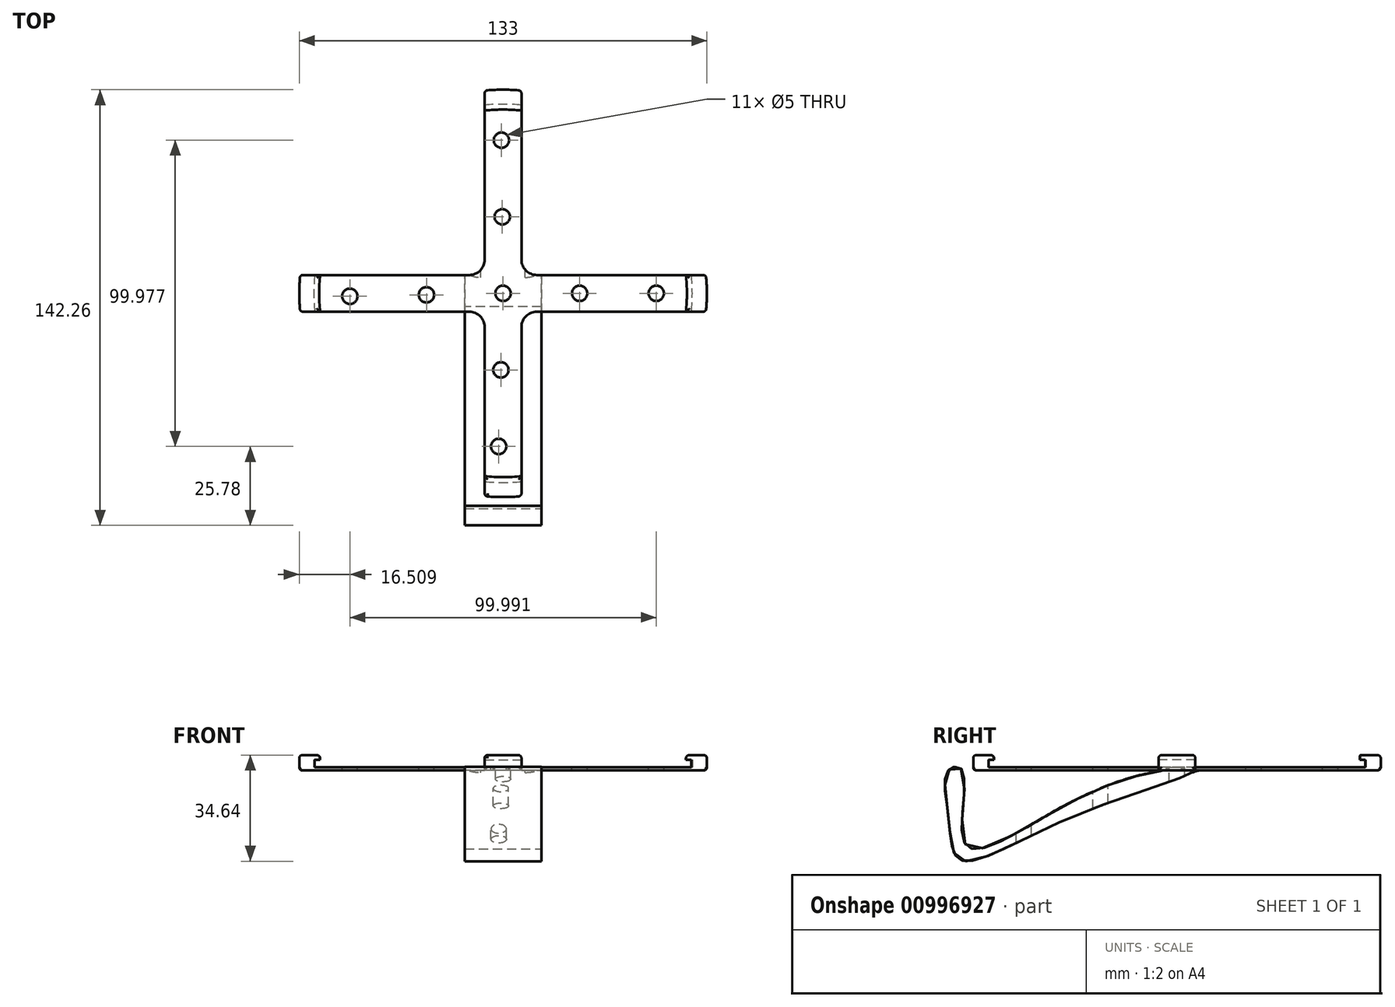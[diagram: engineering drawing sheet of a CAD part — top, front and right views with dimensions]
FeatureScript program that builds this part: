
annotation { "Feature Type Name" : "Feature", "Feature Type Description" : "" }
export const myFeature = defineFeature(function(context is Context, id is Id, definition is map)
    precondition{}
    {
        {
            var Q0;
            Q0=qCreatedBy(makeId("Top.planeOp"),FACE);
            var sketch = newSketch(context, id + "F0", { "sketchPlane" : qUnion([Q0])});
            skCircle(sketch, "E0", {"center": v(0, 0) * mm, "radius": 66.5 * mm, "construction": true});
            skLineSegment(sketch, "E1.bottom", {"start": v(6, -6) * mm, "end": v(-6, -6) * mm, "construction": true});
            skLineSegment(sketch, "E1.top", {"start": v(6, 6) * mm, "end": v(-6, 6) * mm, "construction": true});
            skLineSegment(sketch, "E1.left", {"start": v(6, -6) * mm, "end": v(6, 6) * mm, "construction": true});
            skLineSegment(sketch, "E1.right", {"start": v(-6, -6) * mm, "end": v(-6, 6) * mm, "construction": true});
            skLineSegment(sketch, "E2", {"start": v(-6, 6) * mm, "end": v(-66.23, 6) * mm});
            skLineSegment(sketch, "E3", {"start": v(-6, -6) * mm, "end": v(-66.23, -6) * mm});
            skArc(sketch, "E4", {"start": v(-66.23, 6) * mm, "mid": v(-66.5, 0) * mm, "end": v(-66.23, -6) * mm});
            skLineSegment(sketch, "E5.1.0", {"start": v(-6, -6) * mm, "end": v(-6, -66.23) * mm});
            skLineSegment(sketch, "E5.1.1", {"start": v(6, -6) * mm, "end": v(6, -66.23) * mm});
            skArc(sketch, "E5.1.2", {"start": v(-6, -66.23) * mm, "mid": v(0, -66.5) * mm, "end": v(6, -66.23) * mm});
            skLineSegment(sketch, "E5.2.0", {"start": v(6, -6) * mm, "end": v(66.23, -6) * mm});
            skLineSegment(sketch, "E5.2.1", {"start": v(6, 6) * mm, "end": v(66.23, 6) * mm});
            skArc(sketch, "E5.2.2", {"start": v(66.23, -6) * mm, "mid": v(66.5, 0) * mm, "end": v(66.23, 6) * mm});
            skLineSegment(sketch, "E5.3.0", {"start": v(6, 6) * mm, "end": v(6, 66.23) * mm});
            skLineSegment(sketch, "E5.3.1", {"start": v(-6, 6) * mm, "end": v(-6, 66.23) * mm});
            skArc(sketch, "E5.3.2", {"start": v(6, 66.23) * mm, "mid": v(0, 66.5) * mm, "end": v(-6, 66.23) * mm});
            skSolve(sketch);
        }
        {
            var Q0;
            Q0=qSketchRegion(id+"F0",true);
            extrude(context, id + "F1", {"entities" : qUnion([Q0]), "depth" : 5 * mm, "offsetDistance" : 25 * mm});
        }
        {
            var Q0;
            Q0=makeQuery(id+"F1.opExtrude","CAP_FACE",FACE,{"disambiguationData":[OSD([sQuery(id+"F0.wireOp",EDGE,"E2"),sQuery(id+"F0.wireOp",EDGE,"E3"),sQuery(id+"F0.wireOp",EDGE,"E4"),sQuery(id+"F0.wireOp",EDGE,"E5.1.0"),sQuery(id+"F0.wireOp",EDGE,"E5.1.1"),sQuery(id+"F0.wireOp",EDGE,"E5.1.2"),sQuery(id+"F0.wireOp",EDGE,"E5.2.0"),sQuery(id+"F0.wireOp",EDGE,"E5.2.1"),sQuery(id+"F0.wireOp",EDGE,"E5.2.2"),sQuery(id+"F0.wireOp",EDGE,"E5.3.0"),sQuery(id+"F0.wireOp",EDGE,"E5.3.1"),sQuery(id+"F0.wireOp",EDGE,"E5.3.2")])],"isStart":false});
            var sketch = newSketch(context, id + "F2", { "sketchPlane" : qUnion([Q0])});
            skCircle(sketch, "E6", {"center": v(0, 0) * mm, "radius": 60 * mm, "construction": true});
            skArc(sketch, "E7", {"start": v(-59.7, 6) * mm, "mid": v(-60, 0) * mm, "end": v(-59.7, -6) * mm});
            skLineSegment(sketch, "E8", {"start": v(-59.7, 6) * mm, "end": v(-6, 6) * mm});
            skLineSegment(sketch, "E9", {"start": v(-59.7, -6) * mm, "end": v(-6, -6) * mm});
            skLineSegment(sketch, "E10.1.0", {"start": v(6, -59.7) * mm, "end": v(6, -6) * mm});
            skArc(sketch, "E10.1.1", {"start": v(-6, -59.7) * mm, "mid": v(0, -60) * mm, "end": v(6, -59.7) * mm});
            skLineSegment(sketch, "E10.1.2", {"start": v(-6, -59.7) * mm, "end": v(-6, -6) * mm});
            skLineSegment(sketch, "E10.2.0", {"start": v(59.7, 6) * mm, "end": v(6, 6) * mm});
            skArc(sketch, "E10.2.1", {"start": v(59.7, -6) * mm, "mid": v(60, 0) * mm, "end": v(59.7, 6) * mm});
            skLineSegment(sketch, "E10.2.2", {"start": v(59.7, -6) * mm, "end": v(6, -6) * mm});
            skLineSegment(sketch, "E10.3.0", {"start": v(-6, 59.7) * mm, "end": v(-6, 6) * mm});
            skArc(sketch, "E10.3.1", {"start": v(6, 59.7) * mm, "mid": v(0, 60) * mm, "end": v(-6, 59.7) * mm});
            skLineSegment(sketch, "E10.3.2", {"start": v(6, 59.7) * mm, "end": v(6, 6) * mm});
            skSolve(sketch);
        }
        {
            var Q0;
            Q0=qSketchRegion(id+"F2",true);
            extrude(context, id + "F3", {"entities" : qUnion([Q0]), "operationType" : NewBodyOperationType.REMOVE, "oppositeDirection" : true, "depth" : 4 * mm, "offsetDistance" : 25 * mm});
        }
        {
            var Q0;
            Q0=makeQuery(id+"F3.boolean.opBoolean","COPY",FACE,{"derivedFrom":makeQuery(id+"F3.opExtrude","CAP_FACE",FACE,{"disambiguationData":[OSD([sQuery(id+"F2.wireOp",EDGE,"E7"),sQuery(id+"F2.wireOp",EDGE,"E8"),sQuery(id+"F2.wireOp",EDGE,"E9"),sQuery(id+"F2.wireOp",EDGE,"E10.1.0"),sQuery(id+"F2.wireOp",EDGE,"E10.1.1"),sQuery(id+"F2.wireOp",EDGE,"E10.1.2"),sQuery(id+"F2.wireOp",EDGE,"E10.2.0"),sQuery(id+"F2.wireOp",EDGE,"E10.2.1"),sQuery(id+"F2.wireOp",EDGE,"E10.2.2"),sQuery(id+"F2.wireOp",EDGE,"E10.3.0"),sQuery(id+"F2.wireOp",EDGE,"E10.3.1"),sQuery(id+"F2.wireOp",EDGE,"E10.3.2")])],"isStart":false})});
            var sketch = newSketch(context, id + "F4", { "sketchPlane" : qUnion([Q0])});
            skLineSegment(sketch, "E11.bottom", {"start": v(-6, 6) * mm, "end": v(-64.12, 6) * mm, "construction": true});
            skLineSegment(sketch, "E11.top", {"start": v(-6, -6) * mm, "end": v(-64.12, -6) * mm, "construction": true});
            skLineSegment(sketch, "E11.left", {"start": v(-6, 6) * mm, "end": v(-6, -6) * mm, "construction": true});
            skLineSegment(sketch, "E11.right", {"start": v(-64.12, 6) * mm, "end": v(-64.12, -6) * mm, "construction": true});
            skArc(sketch, "E12", {"start": v(-61.46, 6) * mm, "mid": v(-61.75, 0) * mm, "end": v(-61.46, -6) * mm});
            skLineSegment(sketch, "E13", {"start": v(-61.46, 6) * mm, "end": v(-6, 6) * mm});
            skLineSegment(sketch, "E14", {"start": v(-6, -6) * mm, "end": v(-61.46, -6) * mm});
            skLineSegment(sketch, "E15.1.0", {"start": v(6, -6) * mm, "end": v(6, -61.46) * mm});
            skLineSegment(sketch, "E15.1.1", {"start": v(-6, -61.46) * mm, "end": v(-6, -6) * mm});
            skArc(sketch, "E15.1.2", {"start": v(-6, -61.46) * mm, "mid": v(0, -61.75) * mm, "end": v(6, -61.46) * mm});
            skLineSegment(sketch, "E15.2.0", {"start": v(6, 6) * mm, "end": v(61.46, 6) * mm});
            skLineSegment(sketch, "E15.2.1", {"start": v(61.46, -6) * mm, "end": v(6, -6) * mm});
            skArc(sketch, "E15.2.2", {"start": v(61.46, -6) * mm, "mid": v(61.75, 0) * mm, "end": v(61.46, 6) * mm});
            skLineSegment(sketch, "E15.3.0", {"start": v(-6, 6) * mm, "end": v(-6, 61.46) * mm});
            skLineSegment(sketch, "E15.3.1", {"start": v(6, 61.46) * mm, "end": v(6, 6) * mm});
            skArc(sketch, "E15.3.2", {"start": v(6, 61.46) * mm, "mid": v(0, 61.75) * mm, "end": v(-6, 61.46) * mm});
            skPoint(sketch, "E15.center", {"position": v(0, 0) * mm});
            skSolve(sketch);
        }
        {
            var Q0;
            Q0=qSketchRegion(id+"F4",true);
            extrude(context, id + "F5", {"entities" : qUnion([Q0]), "operationType" : NewBodyOperationType.REMOVE, "depth" : 2.5 * mm, "offsetDistance" : 25 * mm});
        }
        {
            var Q0;
            Q0=makeQuery(id+"F1.opExtrude","SWEPT_EDGE",EDGE,{"disambiguationData":[OSD([sQuery(id+"F0.wireOp",EDGE,"E5.1.1"),sQuery(id+"F0.wireOp",EDGE,"E5.2.0")])]});
            var Q1;
            Q1=makeQuery(id+"F1.opExtrude","SWEPT_EDGE",EDGE,{"disambiguationData":[OSD([sQuery(id+"F0.wireOp",EDGE,"E3"),sQuery(id+"F0.wireOp",EDGE,"E5.1.0")])]});
            var Q2;
            Q2=makeQuery(id+"F1.opExtrude","SWEPT_EDGE",EDGE,{"disambiguationData":[OSD([sQuery(id+"F0.wireOp",EDGE,"E2"),sQuery(id+"F0.wireOp",EDGE,"E5.3.1")])]});
            var Q3;
            Q3=makeQuery(id+"F1.opExtrude","SWEPT_EDGE",EDGE,{"disambiguationData":[OSD([sQuery(id+"F0.wireOp",EDGE,"E5.2.1"),sQuery(id+"F0.wireOp",EDGE,"E5.3.0")])]});
            fillet(context, id + "F6", {"entities" : qUnion([Q0, Q1, Q2, Q3]), "radius" : 5 * mm, "tangentPropagation" : true, "allowEdgeOverflow" : false});
        }
        {
            var Q0;
            Q0=makeQuery(id+"F1.opExtrude","CAP_EDGE",EDGE,{"disambiguationData":[OSD([sQuery(id+"F0.wireOp",EDGE,"E5.3.2")])],"isStart":false});
            var Q1;
            Q1=makeQuery(id+"F3.boolean.opBoolean","COPY",EDGE,{"derivedFrom":makeQuery(id+"F3.opExtrude","CAP_EDGE",EDGE,{"disambiguationData":[OSD([sQuery(id+"F2.wireOp",EDGE,"E10.3.1")])],"isStart":true})});
            var Q2;
            Q2=makeQuery(id+"F1.opExtrude","SWEPT_EDGE",EDGE,{"disambiguationData":[OSD([sQuery(id+"F0.wireOp",EDGE,"E5.3.0"),sQuery(id+"F0.wireOp",EDGE,"E5.3.2")])]});
            var Q3;
            Q3=makeQuery(id+"F1.opExtrude","CAP_EDGE",EDGE,{"disambiguationData":[OSD([sQuery(id+"F0.wireOp",EDGE,"E5.3.0")])],"isStart":false});
            var Q4;
            Q4=makeQuery(id+"F1.opExtrude","CAP_EDGE",EDGE,{"disambiguationData":[OSD([sQuery(id+"F0.wireOp",EDGE,"E5.3.1")])],"isStart":false});
            var Q5;
            Q5=makeQuery(id+"F1.opExtrude","SWEPT_EDGE",EDGE,{"disambiguationData":[OSD([sQuery(id+"F0.wireOp",EDGE,"E5.3.1"),sQuery(id+"F0.wireOp",EDGE,"E5.3.2")])]});
            var Q6;
            Q6=makeQuery(id+"F1.opExtrude","CAP_EDGE",EDGE,{"disambiguationData":[OSD([sQuery(id+"F0.wireOp",EDGE,"E5.3.2")])],"isStart":true});
            var Q7;
            Q7=makeQuery(id+"F1.opExtrude","CAP_EDGE",EDGE,{"disambiguationData":[OSD([sQuery(id+"F0.wireOp",EDGE,"E2")])],"isStart":false});
            var Q8;
            Q8=makeQuery(id+"F3.boolean.opBoolean","COPY",EDGE,{"derivedFrom":makeQuery(id+"F3.opExtrude","CAP_EDGE",EDGE,{"disambiguationData":[OSD([sQuery(id+"F2.wireOp",EDGE,"E7")])],"isStart":true})});
            var Q9;
            Q9=makeQuery(id+"F1.opExtrude","CAP_EDGE",EDGE,{"disambiguationData":[OSD([sQuery(id+"F0.wireOp",EDGE,"E3")])],"isStart":false});
            var Q10;
            Q10=makeQuery(id+"F1.opExtrude","CAP_EDGE",EDGE,{"disambiguationData":[OSD([sQuery(id+"F0.wireOp",EDGE,"E4")])],"isStart":false});
            var Q11;
            Q11=makeQuery(id+"F1.opExtrude","SWEPT_EDGE",EDGE,{"disambiguationData":[OSD([sQuery(id+"F0.wireOp",EDGE,"E3"),sQuery(id+"F0.wireOp",EDGE,"E4")])]});
            var Q12;
            Q12=makeQuery(id+"F1.opExtrude","SWEPT_EDGE",EDGE,{"disambiguationData":[OSD([sQuery(id+"F0.wireOp",EDGE,"E2"),sQuery(id+"F0.wireOp",EDGE,"E4")])]});
            var Q13;
            Q13=makeQuery(id+"F1.opExtrude","SWEPT_EDGE",EDGE,{"disambiguationData":[OSD([sQuery(id+"F0.wireOp",EDGE,"E5.1.0"),sQuery(id+"F0.wireOp",EDGE,"E5.1.2")])]});
            var Q14;
            Q14=makeQuery(id+"F1.opExtrude","CAP_EDGE",EDGE,{"disambiguationData":[OSD([sQuery(id+"F0.wireOp",EDGE,"E5.1.2")])],"isStart":false});
            var Q15;
            Q15=makeQuery(id+"F1.opExtrude","SWEPT_EDGE",EDGE,{"disambiguationData":[OSD([sQuery(id+"F0.wireOp",EDGE,"E5.1.1"),sQuery(id+"F0.wireOp",EDGE,"E5.1.2")])]});
            var Q16;
            Q16=makeQuery(id+"F3.boolean.opBoolean","COPY",EDGE,{"derivedFrom":makeQuery(id+"F3.opExtrude","CAP_EDGE",EDGE,{"disambiguationData":[OSD([sQuery(id+"F2.wireOp",EDGE,"E10.1.1")])],"isStart":true})});
            var Q17;
            Q17=makeQuery(id+"F1.opExtrude","CAP_EDGE",EDGE,{"disambiguationData":[OSD([sQuery(id+"F0.wireOp",EDGE,"E5.1.1")])],"isStart":false});
            var Q18;
            Q18=makeQuery(id+"F1.opExtrude","CAP_EDGE",EDGE,{"disambiguationData":[OSD([sQuery(id+"F0.wireOp",EDGE,"E5.1.0")])],"isStart":false});
            var Q19;
            Q19=makeQuery(id+"F1.opExtrude","SWEPT_EDGE",EDGE,{"disambiguationData":[OSD([sQuery(id+"F0.wireOp",EDGE,"E5.2.1"),sQuery(id+"F0.wireOp",EDGE,"E5.2.2")])]});
            var Q20;
            Q20=makeQuery(id+"F1.opExtrude","CAP_EDGE",EDGE,{"disambiguationData":[OSD([sQuery(id+"F0.wireOp",EDGE,"E5.2.2")])],"isStart":true});
            var Q21;
            Q21=makeQuery(id+"F1.opExtrude","CAP_EDGE",EDGE,{"disambiguationData":[OSD([sQuery(id+"F0.wireOp",EDGE,"E5.2.2")])],"isStart":false});
            var Q22;
            Q22=makeQuery(id+"F1.opExtrude","SWEPT_EDGE",EDGE,{"disambiguationData":[OSD([sQuery(id+"F0.wireOp",EDGE,"E5.2.0"),sQuery(id+"F0.wireOp",EDGE,"E5.2.2")])]});
            var Q23;
            Q23=makeQuery(id+"F1.opExtrude","CAP_EDGE",EDGE,{"disambiguationData":[OSD([sQuery(id+"F0.wireOp",EDGE,"E5.2.1")])],"isStart":false});
            var Q24;
            Q24=makeQuery(id+"F3.boolean.opBoolean","COPY",EDGE,{"derivedFrom":makeQuery(id+"F3.opExtrude","CAP_EDGE",EDGE,{"disambiguationData":[OSD([sQuery(id+"F2.wireOp",EDGE,"E10.2.1")])],"isStart":true})});
            var Q25;
            Q25=makeQuery(id+"F1.opExtrude","CAP_EDGE",EDGE,{"disambiguationData":[OSD([sQuery(id+"F0.wireOp",EDGE,"E5.2.0")])],"isStart":false});
            var Q26;
            Q26=makeQuery(id+"F1.opExtrude","CAP_EDGE",EDGE,{"disambiguationData":[OSD([sQuery(id+"F0.wireOp",EDGE,"E4")])],"isStart":true});
            var Q27;
            Q27=makeQuery(id+"F1.opExtrude","CAP_EDGE",EDGE,{"disambiguationData":[OSD([sQuery(id+"F0.wireOp",EDGE,"E5.1.2")])],"isStart":true});
            fillet(context, id + "F7", {"entities" : qUnion([Q0, Q1, Q2, Q3, Q4, Q5, Q6, Q7, Q8, Q9, Q10, Q11, Q12, Q13, Q14, Q15, Q16, Q17, Q18, Q19, Q20, Q21, Q22, Q23, Q24, Q25, Q26, Q27]), "radius" : 1 * mm, "tangentPropagation" : true, "allowEdgeOverflow" : false});
        }
        {
            var Q0;
            Q0=qCreatedBy(makeId("Right.planeOp"),FACE);
            var sketch = newSketch(context, id + "F8", { "sketchPlane" : qUnion([Q0])});
            skLineSegment(sketch, "E16.bottom", {"start": v(0, 0) * mm, "end": v(-74.6, 0) * mm, "construction": true});
            skLineSegment(sketch, "E16.top", {"start": v(0, -30.56) * mm, "end": v(-74.6, -30.56) * mm, "construction": true});
            skLineSegment(sketch, "E16.left", {"start": v(0, 0) * mm, "end": v(0, -30.56) * mm, "construction": true});
            skLineSegment(sketch, "E16.right", {"start": v(-74.6, 0) * mm, "end": v(-74.6, -30.56) * mm, "construction": true});
            skLineSegment(sketch, "E17.bottom", {"start": v(5.94, 0) * mm, "end": v(0, 0) * mm, "construction": true});
            skLineSegment(sketch, "E17.top", {"start": v(5.94, -30.56) * mm, "end": v(0, -30.56) * mm, "construction": true});
            skLineSegment(sketch, "E17.left", {"start": v(5.94, 0) * mm, "end": v(5.94, -30.56) * mm, "construction": true});
            skLineSegment(sketch, "E18", {"start": v(5.94, 0) * mm, "end": v(-74.6, -30.56) * mm, "construction": true});
            skLineSegment(sketch, "E19", {"start": v(5.94, -30.56) * mm, "end": v(-74.6, 0) * mm, "construction": true});
            skLineSegment(sketch, "E20.MirrorCS", {"start": v(-5.94, 0) * mm, "end": v(-5.94, -30.56) * mm, "construction": true});
            skLineSegment(sketch, "E21", {"start": v(21.4, -15.28) * mm, "end": v(-74.6, -15.28) * mm, "construction": true});
            skPoint(sketch, "E21.startSnap0", {"position": v(5.94, -15.28) * mm});
            skLineSegment(sketch, "E22", {"start": v(-5.52, -0.17) * mm, "end": v(-86.06, -30.73) * mm, "construction": true});
            skFitSpline(sketch, "E23", {"points": [v(5.94, 0) * mm, v(-35.36, -15.67) * mm, v(-70.87, -29.14) * mm, v(-74.6, -15.28) * mm, v(-74.6, 0) * mm, v(-70.07, 0) * mm, v(-69.01, -24.26) * mm, v(-39.84, -13.19) * mm, v(-5.52, -0.17) * mm, v(5.94, 0) * mm]});
            skSolve(sketch);
        }
        {
            var Q0;
            Q0 = qSketchRegion(id + "F8", true);
            extrude(context, id + "F9", {"entities" : qUnion([Q0]), "operationType" : NewBodyOperationType.ADD, "endBound" : BoundingType.SYMMETRIC, "depth" : 25 * mm, "offsetDistance" : 25 * mm});
        }
        {
            var Q0;
            Q0=makeQuery(id+"F9.boolean.opBoolean","INTERSECT",EDGE,{"disambiguationData":[OD(1.0)],"derivedFrom":[makeQuery(id+"F1.opExtrude","CAP_FACE",FACE,{"disambiguationData":[OSD([sQuery(id+"F0.wireOp",EDGE,"E2"),sQuery(id+"F0.wireOp",EDGE,"E3"),sQuery(id+"F0.wireOp",EDGE,"E4"),sQuery(id+"F0.wireOp",EDGE,"E5.1.0"),sQuery(id+"F0.wireOp",EDGE,"E5.1.1"),sQuery(id+"F0.wireOp",EDGE,"E5.1.2"),sQuery(id+"F0.wireOp",EDGE,"E5.2.0"),sQuery(id+"F0.wireOp",EDGE,"E5.2.1"),sQuery(id+"F0.wireOp",EDGE,"E5.2.2"),sQuery(id+"F0.wireOp",EDGE,"E5.3.0"),sQuery(id+"F0.wireOp",EDGE,"E5.3.1"),sQuery(id+"F0.wireOp",EDGE,"E5.3.2")])],"isStart":true}),makeQuery(id+"F9.opExtrude","SWEPT_FACE",FACE,{"disambiguationData":[OSD([sQuery(id+"F8.wireOp",EDGE,"E23")])]})]});
            fillet(context, id + "F10", {"entities" : qUnion([Q0]), "radius" : 5 * mm, "tangentPropagation" : true, "allowEdgeOverflow" : false});
        }
        {
            var Q0;
            Q0=qCreatedBy(makeId("Top.planeOp"),FACE);
            var sketch = newSketch(context, id + "F11", { "sketchPlane" : qUnion([Q0])});
            skCircle(sketch, "E24", {"center": v(0, 0) * mm, "radius": 2.5 * mm});
            skCircle(sketch, "E25.0.1.0", {"center": v(-0.26, 25) * mm, "radius": 2.5 * mm});
            skCircle(sketch, "E25.0.2.0", {"center": v(-0.52, 50) * mm, "radius": 2.5 * mm});
            skCircle(sketch, "E25.1.0.0", {"center": v(25, 0) * mm, "radius": 2.5 * mm});
            skCircle(sketch, "E25.1.1.0", {"center": v(24.74, 25) * mm, "radius": 2.5 * mm});
            skCircle(sketch, "E25.1.2.0", {"center": v(24.48, 50) * mm, "radius": 2.5 * mm});
            skCircle(sketch, "E25.2.0.0", {"center": v(50, 0) * mm, "radius": 2.5 * mm});
            skCircle(sketch, "E25.2.1.0", {"center": v(49.74, 25) * mm, "radius": 2.5 * mm});
            skCircle(sketch, "E25.2.2.0", {"center": v(49.48, 50) * mm, "radius": 2.5 * mm});
            skLineSegment(sketch, "E25.direction1", {"start": v(0, 0) * mm, "end": v(25, 0) * mm, "construction": true});
            skLineSegment(sketch, "E25.direction2", {"start": v(0, 0) * mm, "end": v(-0.26, 25) * mm, "construction": true});
            skCircle(sketch, "E26.0.1.0", {"center": v(-0.71, -24.99) * mm, "radius": 2.5 * mm});
            skCircle(sketch, "E26.0.2.0", {"center": v(-1.43, -49.98) * mm, "radius": 2.5 * mm});
            skCircle(sketch, "E26.1.0.0", {"center": v(-25, -0.48) * mm, "radius": 2.5 * mm});
            skCircle(sketch, "E26.1.1.0", {"center": v(-25.7, -25.47) * mm, "radius": 2.5 * mm});
            skCircle(sketch, "E26.1.2.0", {"center": v(-26.42, -50.46) * mm, "radius": 2.5 * mm});
            skCircle(sketch, "E26.2.0.0", {"center": v(-50, -0.95) * mm, "radius": 2.5 * mm});
            skCircle(sketch, "E26.2.1.0", {"center": v(-50.7, -25.94) * mm, "radius": 2.5 * mm});
            skCircle(sketch, "E26.2.2.0", {"center": v(-51.42, -50.93) * mm, "radius": 2.5 * mm});
            skLineSegment(sketch, "E26.direction1", {"start": v(0, 0) * mm, "end": v(-25, -0.48) * mm, "construction": true});
            skLineSegment(sketch, "E26.direction2", {"start": v(0, 0) * mm, "end": v(-0.71, -24.99) * mm, "construction": true});
            skSolve(sketch);
        }
        {
            var Q0;
            Q0 = qSketchRegion(id + "F11", true);
            extrude(context, id + "F12", {"entities" : qUnion([Q0]), "operationType" : NewBodyOperationType.REMOVE, "endBound" : BoundingType.SYMMETRIC, "oppositeDirection" : true, "depth" : 50 * mm, "offsetDistance" : 25 * mm});
        }
    });
